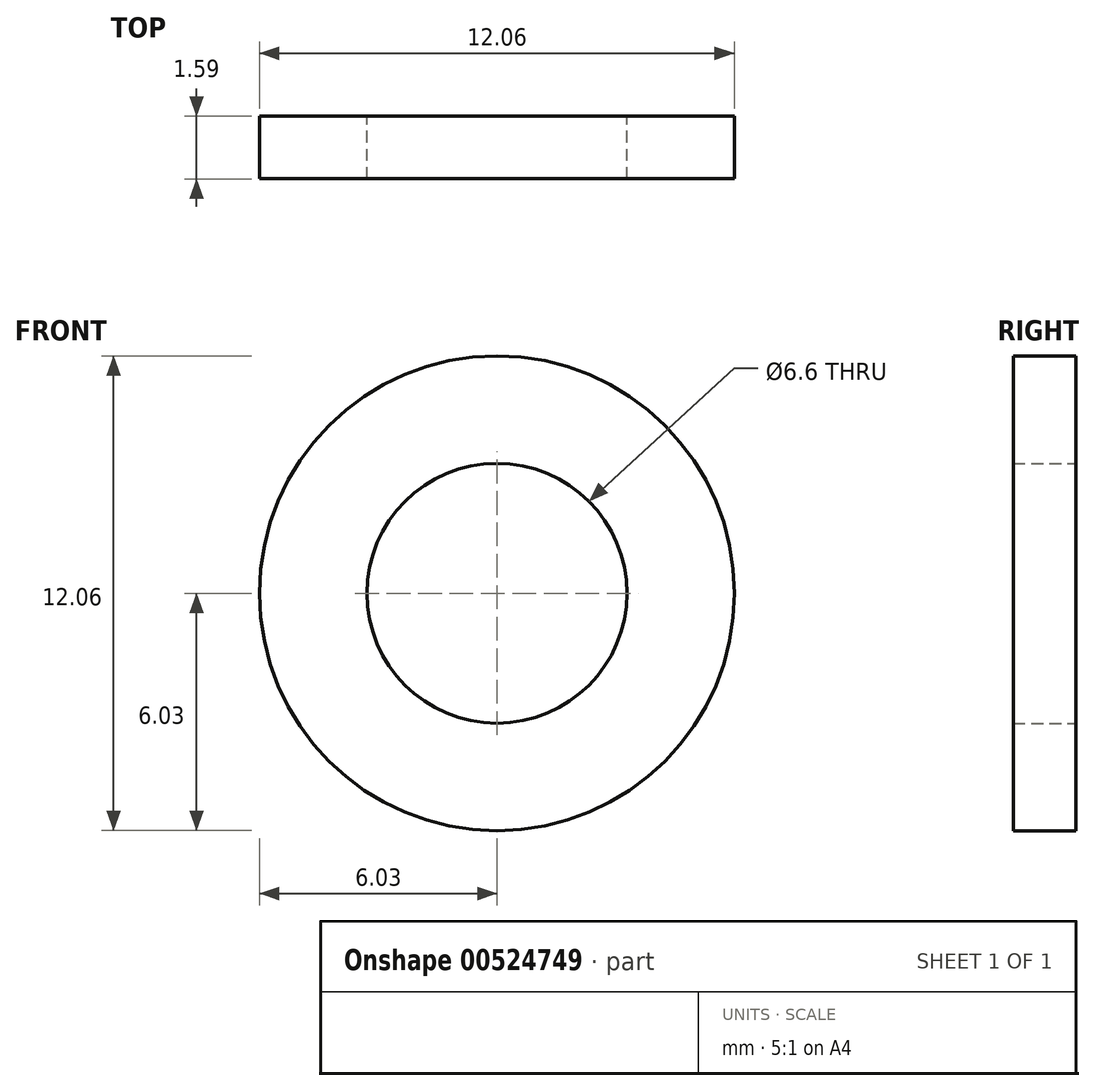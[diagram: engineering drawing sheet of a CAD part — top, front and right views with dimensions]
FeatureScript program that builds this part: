
annotation { "Feature Type Name" : "Feature", "Feature Type Description" : "" }
export const myFeature = defineFeature(function(context is Context, id is Id, definition is map)
    precondition{}
    {
        {
            var Q0;
            Q0=qCreatedBy(makeId("Front.planeOp"),FACE);
            var sketch = newSketch(context, id + "F0", { "sketchPlane" : qUnion([Q0])});
            skCircle(sketch, "E0", {"center": v(0, 0) * mm, "radius": 3.3 * mm});
            skCircle(sketch, "E1", {"center": v(0, 0) * mm, "radius": 6.03 * mm});
            skSolve(sketch);
        }
        {
            var Q0;
            Q0 = qSketchRegion(id + "F0", true);
            extrude(context, id + "F1", {"entities" : qUnion([Q0]), "depth" : 1.59 * mm, "offsetDistance" : 25.4 * mm});
        }
    });
